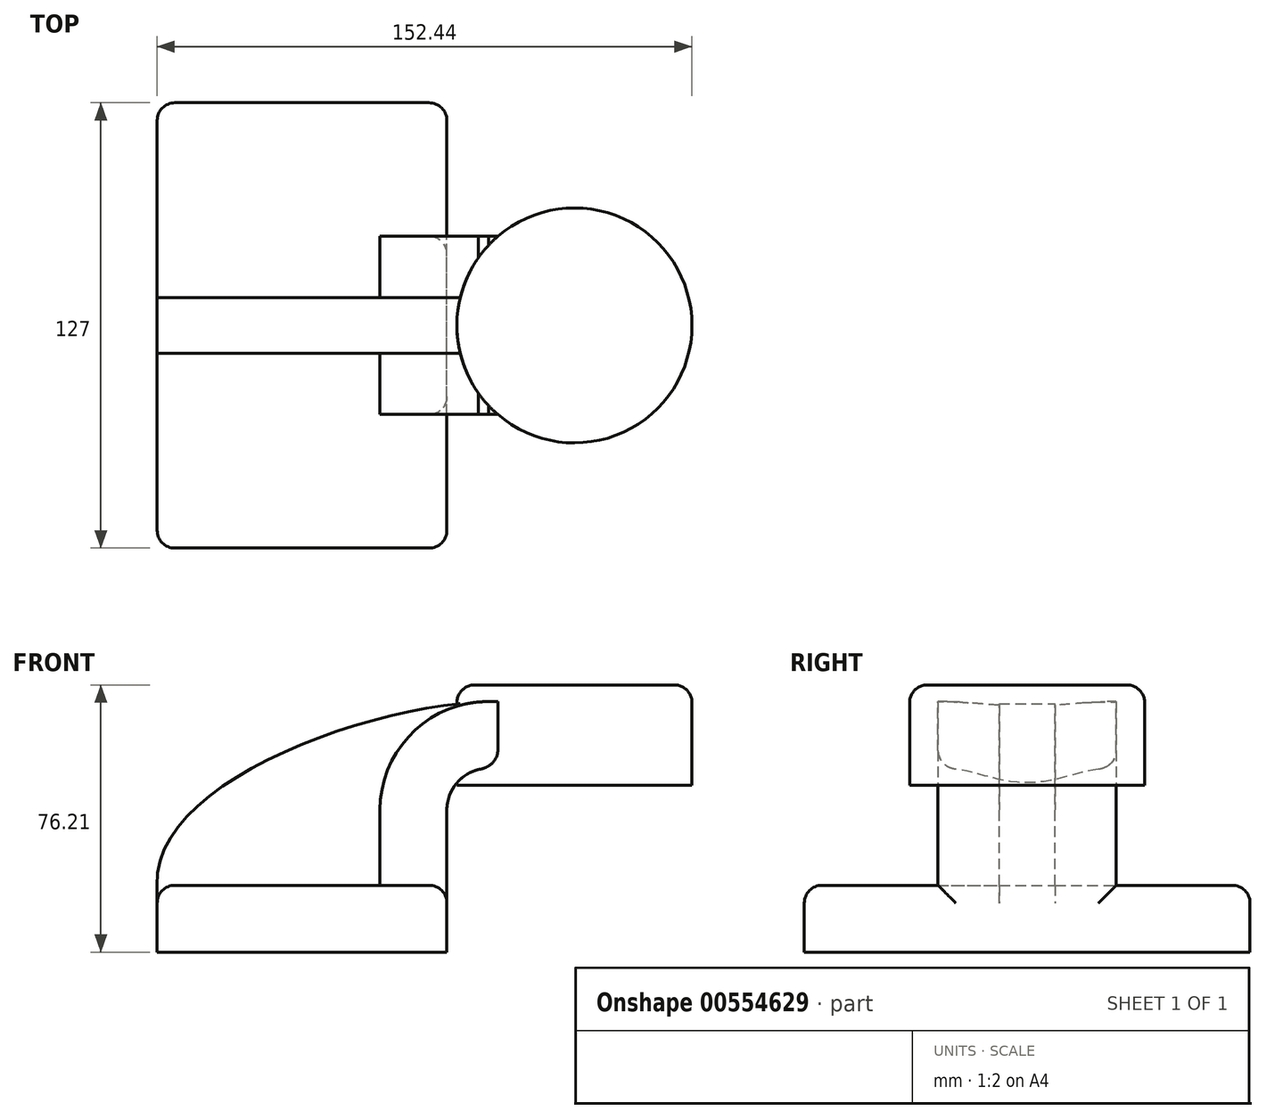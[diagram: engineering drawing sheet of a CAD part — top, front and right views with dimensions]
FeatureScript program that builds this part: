
annotation { "Feature Type Name" : "Feature", "Feature Type Description" : "" }
export const myFeature = defineFeature(function(context is Context, id is Id, definition is map)
    precondition{}
    {
        {
            var Q0;
            Q0=qCreatedBy(makeId("Front.planeOp"),FACE);
            var sketch = newSketch(context, id + "F0", { "sketchPlane" : qUnion([Q0])});
            skLineSegment(sketch, "E0.bottom", {"start": v(-41.27, -9.53) * mm, "end": v(41.28, -9.53) * mm});
            skLineSegment(sketch, "E0.top", {"start": v(-41.28, 9.52) * mm, "end": v(41.28, 9.52) * mm});
            skLineSegment(sketch, "E0.left", {"start": v(-41.28, -9.53) * mm, "end": v(-41.28, 9.52) * mm});
            skLineSegment(sketch, "E0.right", {"start": v(41.28, -9.53) * mm, "end": v(41.28, 9.52) * mm});
            skPoint(sketch, "E0.middle", {"position": v(0, 0) * mm});
            skLineSegment(sketch, "E1.bottom", {"start": v(60.33, 38.1) * mm, "end": v(111.12, 38.1) * mm});
            skLineSegment(sketch, "E1.top", {"start": v(60.33, 66.67) * mm, "end": v(111.12, 66.67) * mm});
            skLineSegment(sketch, "E1.left", {"start": v(60.33, 38.1) * mm, "end": v(60.33, 66.67) * mm});
            skLineSegment(sketch, "E1.right", {"start": v(111.12, 38.1) * mm, "end": v(111.12, 66.67) * mm});
            skPoint(sketch, "E1.middle", {"position": v(85.72, 52.39) * mm});
            skLineSegment(sketch, "E2", {"start": v(41.27, 9.52) * mm, "end": v(41.27, 31) * mm});
            skArc(sketch, "E3", {"start": v(41.28, 31) * mm, "mid": v(44.75, 39.4) * mm, "end": v(53.15, 42.88) * mm});
            skLineSegment(sketch, "E4", {"start": v(53.15, 42.88) * mm, "end": v(77.63, 42.88) * mm});
            skLineSegment(sketch, "E5.0", {"start": v(53.15, 61.93) * mm, "end": v(77.63, 61.93) * mm});
            skArc(sketch, "E5.1", {"start": v(22.23, 31) * mm, "mid": v(31.28, 52.87) * mm, "end": v(53.15, 61.93) * mm});
            skLineSegment(sketch, "E5.2", {"start": v(22.22, 9.52) * mm, "end": v(22.22, 31) * mm});
            skLineSegment(sketch, "E6", {"start": v(77.63, 66.67) * mm, "end": v(77.63, 38.1) * mm});
            skFitSpline(sketch, "E7", {"points": [v(-41.27, 9.53) * mm, v(53.15, 61.93) * mm], "startDerivative": vector(-4.72, 86.83) * mm, "endDerivative": vector(107.24, 3.52) * mm});
            skSolve(sketch);
        }
        {
            var Q0;
            Q0=makeQuery(id+"F0.imprint","IMPRINT",FACE,{"disambiguationData":[TD([[makeQuery(id+"F0.imprint","IMPRINT",EDGE,{"derivedFrom":sQuery(id+"F0.wireOp",EDGE,"E0.bottom")}),1.0]])]});
            extrude(context, id + "F1", {"entities" : qUnion([Q0]), "endBound" : BoundingType.SYMMETRIC, "depth" : 127 * mm, "offsetDistance" : 25.4 * mm});
        }
        {
            var Q0;
            {var subQ1=sQuery(id+"F0.wireOp",EDGE,"E2");Q0=makeQuery(id+"F0.imprint","IMPRINT",FACE,{"disambiguationData":[TD([[makeQuery(id+"F0.imprint","IMPRINT",EDGE,{"derivedFrom":subQ1}),1.0]])]});}
            var Q1;
            {var subQ0=sQuery(id+"F0.wireOp",EDGE,"E4");var subQ1=sQuery(id+"F0.wireOp",EDGE,"E1.left");var subQ2=makeQuery(id+"F0.imprint","INTERSECT",VERTEX,{"derivedFrom":[subQ1,subQ0]});Q1=makeQuery(id+"F0.imprint","IMPRINT",FACE,{"disambiguationData":[TD([[makeQuery(id+"F0.imprint","IMPRINT",EDGE,{"disambiguationData":[TD([[subQ2,-1.0]])],"derivedFrom":subQ1}),-1.0]])]});}
            extrude(context, id + "F2", {"entities" : qUnion([Q0, Q1]), "operationType" : NewBodyOperationType.ADD, "endBound" : BoundingType.SYMMETRIC, "depth" : 50.8 * mm, "offsetDistance" : 25.4 * mm});
        }
        {
            var Q0;
            {var subQ3=sQuery(id+"F0.wireOp",EDGE,"E5.2");Q0=makeQuery(id+"F0.imprint","IMPRINT",FACE,{"disambiguationData":[TD([[makeQuery(id+"F0.imprint","IMPRINT",EDGE,{"derivedFrom":subQ3}),1.0]])]});}
            extrude(context, id + "F3", {"entities" : qUnion([Q0]), "operationType" : NewBodyOperationType.ADD, "endBound" : BoundingType.SYMMETRIC, "depth" : 15.88 * mm, "offsetDistance" : 25.4 * mm});
        }
        {
            var Q0;
            {var subQ4=sQuery(id+"F0.wireOp",EDGE,"E1.right");Q0=makeQuery(id+"F0.imprint","IMPRINT",FACE,{"disambiguationData":[TD([[makeQuery(id+"F0.imprint","IMPRINT",EDGE,{"derivedFrom":subQ4}),1.0]])]});}
            var Q1;
            Q1=sQuery(id+"F0.wireOp",EDGE,"E6");
            revolve(context, id + "F4", {"operationType" : NewBodyOperationType.ADD, "entities" : qUnion([Q0]), "axis" : qUnion([Q1]), "revolveType" : RevolveType.FULL});
        }
        {
            var Q0;
            Q0=makeQuery(id+"F1.opExtrude","CAP_EDGE",EDGE,{"disambiguationData":[OSD([sQuery(id+"F0.wireOp",EDGE,"E0.right")])],"isStart":false});
            var Q1;
            Q1=makeQuery(id+"F1.opExtrude","CAP_EDGE",EDGE,{"disambiguationData":[OSD([sQuery(id+"F0.wireOp",EDGE,"E0.left")])],"isStart":false});
            var Q2;
            Q2=makeQuery(id+"F1.opExtrude","CAP_EDGE",EDGE,{"disambiguationData":[OSD([sQuery(id+"F0.wireOp",EDGE,"E0.right")])],"isStart":true});
            var Q3;
            Q3=makeQuery(id+"F1.opExtrude","CAP_EDGE",EDGE,{"disambiguationData":[OSD([sQuery(id+"F0.wireOp",EDGE,"E0.left")])],"isStart":true});
            fillet(context, id + "F5", {"entities" : qUnion([Q0, Q1, Q2, Q3]), "radius" : 5.08 * mm, "tangentPropagation" : true, "allowEdgeOverflow" : false});
        }
        {
            var Q0;
            Q0=makeQuery(id+"F4.opRevolve","SWEPT_EDGE",EDGE,{"disambiguationData":[OSD([sQuery(id+"F0.wireOp",EDGE,"E1.top"),sQuery(id+"F0.wireOp",EDGE,"E1.right")])]});
            fillet(context, id + "F6", {"entities" : qUnion([Q0]), "radius" : 5.08 * mm, "tangentPropagation" : true, "allowEdgeOverflow" : false});
        }
        {
            var Q0;
            Q0=makeQuery(id+"F2.opExtrude","CAP_EDGE",EDGE,{"disambiguationData":[OSD([sQuery(id+"F0.wireOp",EDGE,"E3")])],"isStart":false});
            fillet(context, id + "F7", {"entities" : qUnion([Q0]), "radius" : 5.08 * mm, "tangentPropagation" : true, "allowEdgeOverflow" : false});
        }
        {
            var Q0;
            Q0=makeQuery(id+"F1.opExtrude","CAP_EDGE",EDGE,{"disambiguationData":[OSD([sQuery(id+"F0.wireOp",EDGE,"E0.top")])],"isStart":false});
            fillet(context, id + "F8", {"entities" : qUnion([Q0]), "radius" : 5.08 * mm, "tangentPropagation" : true, "allowEdgeOverflow" : false});
        }
        {
            var Q0;
            {var subQ0=sQuery(id+"F0.wireOp",EDGE,"E2");var subQ1=sQuery(id+"F0.wireOp",EDGE,"E0.top");var subQ2=sQuery(id+"F0.wireOp",EDGE,"E0.right");Q0=makeQuery(id+"F2.boolean.opBoolean","SPLIT",EDGE,{"disambiguationData":[TD([makeQuery(id+"F1.opExtrude","CAP_FACE",FACE,{"disambiguationData":[OSD([sQuery(id+"F0.wireOp",EDGE,"E0.bottom"),subQ1,sQuery(id+"F0.wireOp",EDGE,"E0.left"),subQ2])],"isStart":true})])],"derivedFrom":makeQuery(id+"F1.opExtrude","SWEPT_EDGE",EDGE,{"disambiguationData":[OSD([subQ1,subQ2,subQ0])]})});}
            fillet(context, id + "F9", {"entities" : qUnion([Q0]), "radius" : 5.08 * mm, "tangentPropagation" : true, "allowEdgeOverflow" : false});
        }
        {
            var Q0;
            Q0=makeQuery(id+"F2.opExtrude","CAP_EDGE",EDGE,{"disambiguationData":[OSD([sQuery(id+"F0.wireOp",EDGE,"E3")])],"isStart":true});
            fillet(context, id + "F10", {"entities" : qUnion([Q0]), "radius" : 5.08 * mm, "tangentPropagation" : true, "allowEdgeOverflow" : false});
        }
    });
